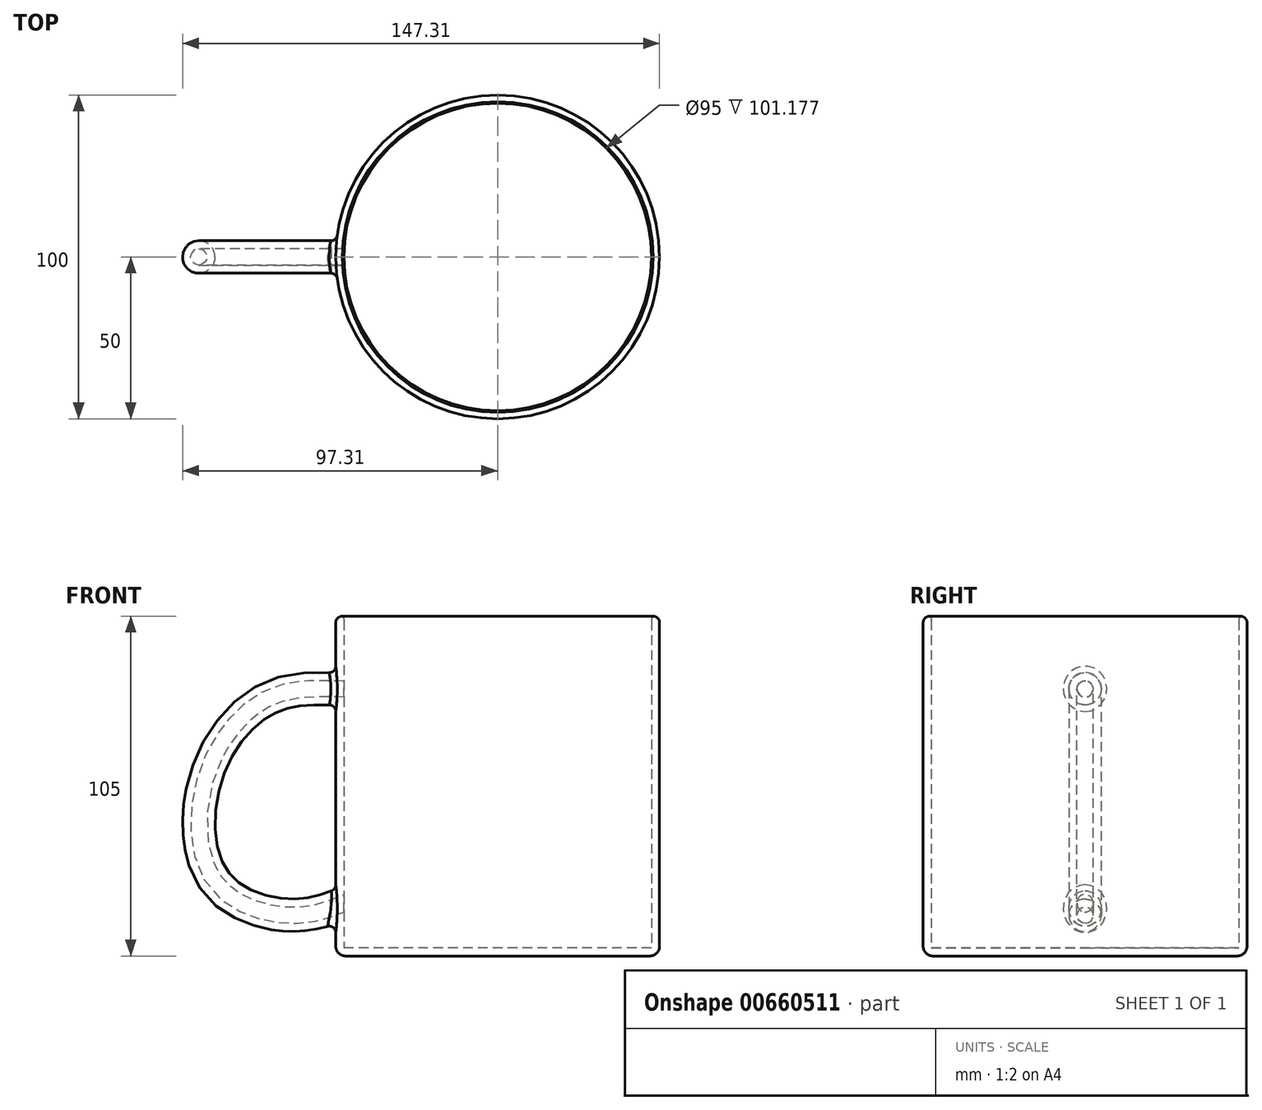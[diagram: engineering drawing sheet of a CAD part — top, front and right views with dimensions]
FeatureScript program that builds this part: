
annotation { "Feature Type Name" : "Feature", "Feature Type Description" : "" }
export const myFeature = defineFeature(function(context is Context, id is Id, definition is map)
    precondition{}
    {
        {
            var Q0;
            Q0=qCreatedBy(makeId("Top.planeOp"),FACE);
            var sketch = newSketch(context, id + "F0", { "sketchPlane" : qUnion([Q0])});
            skCircle(sketch, "E0", {"center": v(0, 0) * mm, "radius": 50 * mm});
            skSolve(sketch);
        }
        {
            var Q0;
            Q0 = qSketchRegion(id + "F0", true);
            extrude(context, id + "F1", {"entities" : qUnion([Q0]), "depth" : 105 * mm, "offsetDistance" : 25 * mm});
        }
        {
            var Q0;
            Q0=qCreatedBy(makeId("Right.planeOp"),FACE);
            cPlane(context, id + "F2", {"entities" : qUnion([Q0]), "cplaneType" : CPlaneType.OFFSET, "offset" : 50 * mm, "oppositeDirection" : true, "width" : 150 * mm, "height" : 150 * mm});
        }
        {
            var Q0;
            Q0=qCreatedBy(makeId("Front.planeOp"),FACE);
            var sketch = newSketch(context, id + "F3", { "sketchPlane" : qUnion([Q0])});
            skFitSpline(sketch, "E1", {"points": [v(-49.7, 84.98) * mm, v(-71.79, 81.9) * mm, v(-92.03, 57.37) * mm, v(-88.97, 21.17) * mm, v(-62.58, 10.12) * mm, v(-44.18, 15.03) * mm], "startDerivative": vector(-124.4, 2.53) * mm, "endDerivative": vector(100.17, 42.88) * mm});
            skSolve(sketch);
        }
        {
            var Q0;
            Q0=qCreatedBy(id+"F2.planeOp",FACE);
            var sketch = newSketch(context, id + "F4", { "sketchPlane" : qUnion([Q0])});
            skCircle(sketch, "E2", {"center": v(0, 82.52) * mm, "radius": 5 * mm});
            skSolve(sketch);
        }
        {
            var Q0;
            Q0=makeQuery(id+"F4.imprint","IMPRINT",FACE,{"disambiguationData":[TD([[makeQuery(id+"F4.imprint","IMPRINT",EDGE,{"derivedFrom":sQuery(id+"F4.wireOp",EDGE,"E2")}),1.0]])]});
            var Q1;
            Q1=sQuery(id+"F3.wireOp",EDGE,"E1");
            sweep(context, id + "F5", {"operationType" : NewBodyOperationType.ADD, "profiles" : qUnion([Q0]), "path" : qUnion([Q1])});
        }
        {
            var Q0;
            Q0=makeQuery(id+"F1.opExtrude","CAP_FACE",FACE,{"disambiguationData":[OSD([sQuery(id+"F0.wireOp",EDGE,"E0")])],"isStart":false});
            shell(context, id + "F6", {"entities" : qUnion([Q0]), "thickness" : 2.5 * mm});
        }
        {
            var Q0;
            Q0=makeQuery(id+"F1.opExtrude","CAP_EDGE",EDGE,{"disambiguationData":[OSD([sQuery(id+"F0.wireOp",EDGE,"E0")])],"isStart":false});
            fillet(context, id + "F7", {"entities" : qUnion([Q0]), "radius" : 2 * mm, "tangentPropagation" : true, "allowEdgeOverflow" : false});
        }
        {
            var Q0;
            {var subQ0=sQuery(id+"F0.wireOp",EDGE,"E0");Q0=makeQuery(id+"F6.opShell","OFFSET_EDGE",EDGE,{"disambiguationData":[OSD([subQ0]),TDD([makeQuery(id+"F1.opExtrude","CAP_EDGE",EDGE,{"disambiguationData":[OSD([subQ0])],"isStart":false})])]});}
            fillet(context, id + "F8", {"entities" : qUnion([Q0]), "radius" : 2 * mm, "tangentPropagation" : true, "allowEdgeOverflow" : false});
        }
        {
            var Q0;
            Q0=makeQuery(id+"F1.opExtrude","CAP_EDGE",EDGE,{"disambiguationData":[OSD([sQuery(id+"F0.wireOp",EDGE,"E0")])],"isStart":true});
            fillet(context, id + "F9", {"entities" : qUnion([Q0]), "radius" : 3 * mm, "tangentPropagation" : true, "allowEdgeOverflow" : false});
        }
        {
            var Q0;
            Q0=makeQuery(id+"F5.boolean.opBoolean","INTERSECT",EDGE,{"disambiguationData":[OD(1.0)],"derivedFrom":[makeQuery(id+"F1.opExtrude","SWEPT_FACE",FACE,{"disambiguationData":[OSD([sQuery(id+"F0.wireOp",EDGE,"E0")])]}),makeQuery(id+"F5.opSweep","SWEPT_FACE",FACE,{"disambiguationData":[OSD([sQuery(id+"F3.wireOp",EDGE,"E1"),sQuery(id+"F4.wireOp",EDGE,"E2")])]})]});
            fillet(context, id + "F10", {"entities" : qUnion([Q0]), "radius" : 2 * mm, "tangentPropagation" : true, "allowEdgeOverflow" : false});
        }
        {
            var Q0;
            Q0=makeQuery(id+"F5.boolean.opBoolean","INTERSECT",EDGE,{"disambiguationData":[OD(0.0)],"derivedFrom":[makeQuery(id+"F1.opExtrude","SWEPT_FACE",FACE,{"disambiguationData":[OSD([sQuery(id+"F0.wireOp",EDGE,"E0")])]}),makeQuery(id+"F5.opSweep","SWEPT_FACE",FACE,{"disambiguationData":[OSD([sQuery(id+"F3.wireOp",EDGE,"E1"),sQuery(id+"F4.wireOp",EDGE,"E2")])]})]});
            fillet(context, id + "F11", {"entities" : qUnion([Q0]), "radius" : 2 * mm, "tangentPropagation" : true, "allowEdgeOverflow" : false});
        }
    });
